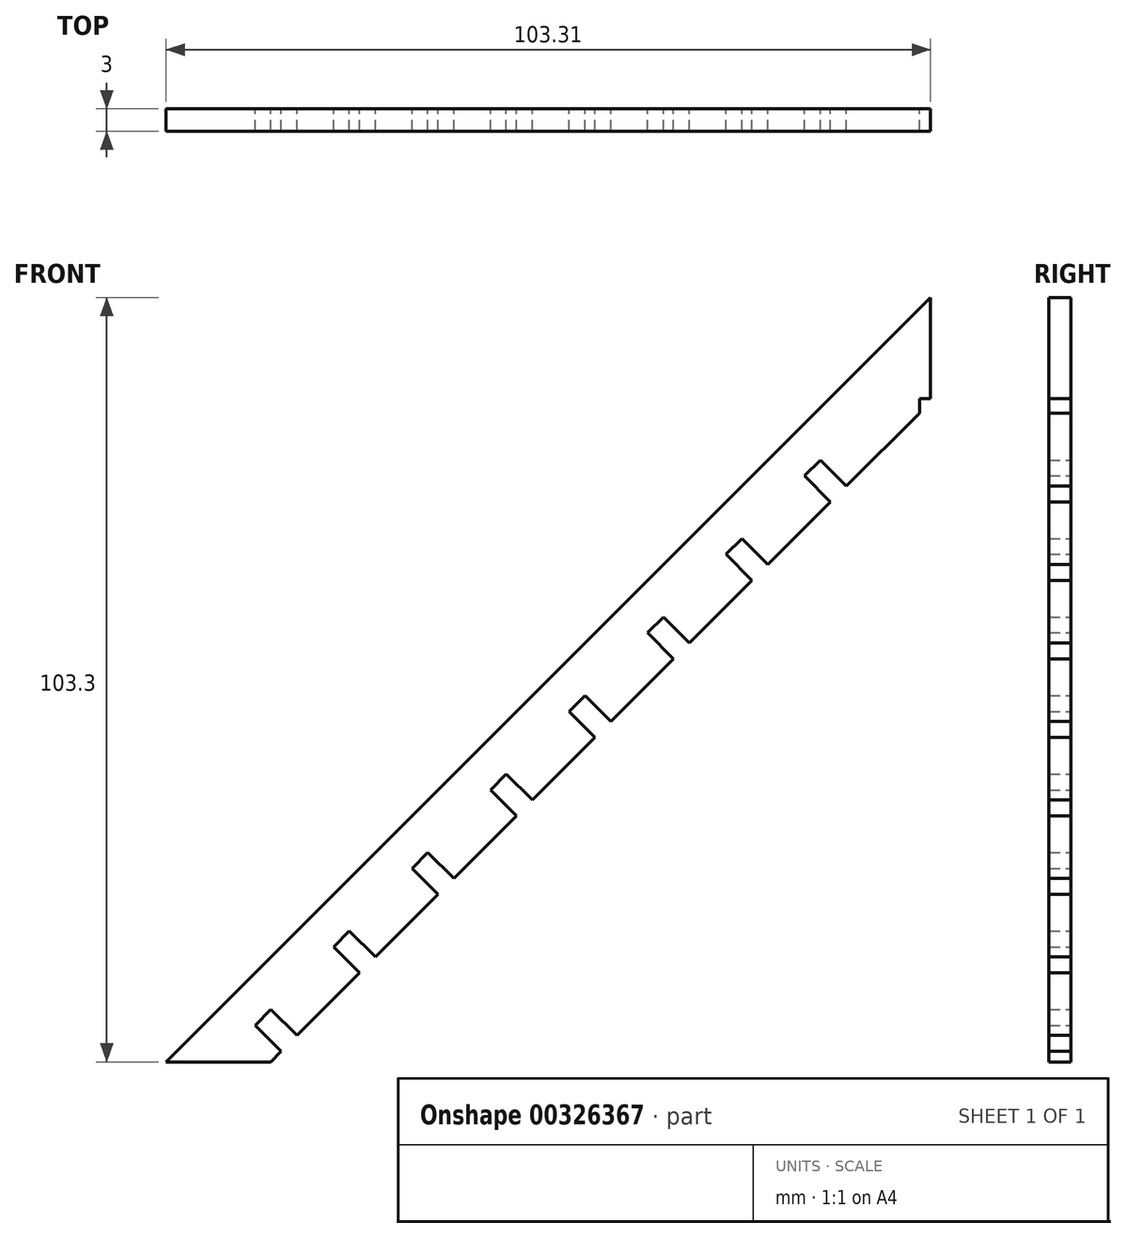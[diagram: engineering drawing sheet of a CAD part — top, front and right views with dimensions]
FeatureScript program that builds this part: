
annotation { "Feature Type Name" : "Feature", "Feature Type Description" : "" }
export const myFeature = defineFeature(function(context is Context, id is Id, definition is map)
    precondition{}
    {
        {
            var Q0;
            Q0=qCreatedBy(makeId("Front.planeOp"),FACE);
            var sketch = newSketch(context, id + "F0", { "sketchPlane" : qUnion([Q0])});
            skLineSegment(sketch, "E0", {"start": v(-78.64, 4.95) * mm, "end": v(-75.1, 1.42) * mm});
            skLineSegment(sketch, "E1", {"start": v(-68.04, 15.56) * mm, "end": v(-64.5, 12.02) * mm});
            skPoint(sketch, "E2", {"position": v(-57.43, 26.16) * mm});
            skPoint(sketch, "E3", {"position": v(-46.82, 36.77) * mm});
            skPoint(sketch, "E4", {"position": v(-36.22, 47.38) * mm});
            skPoint(sketch, "E5", {"position": v(-25.61, 57.98) * mm});
            skPoint(sketch, "E6", {"position": v(-15, 68.59) * mm});
            skPoint(sketch, "E7", {"position": v(-4.4, 79.2) * mm});
            skLineSegment(sketch, "E8", {"start": v(-72.96, 3.56) * mm, "end": v(-76.5, 7.1) * mm});
            skLineSegment(sketch, "E9", {"start": v(-57.43, 26.16) * mm, "end": v(-53.9, 22.63) * mm});
            skLineSegment(sketch, "E10", {"start": v(-46.82, 36.77) * mm, "end": v(-43.29, 33.23) * mm});
            skLineSegment(sketch, "E11", {"start": v(-36.22, 47.38) * mm, "end": v(-32.68, 43.84) * mm});
            skLineSegment(sketch, "E12", {"start": v(-25.61, 57.98) * mm, "end": v(-22.08, 54.45) * mm});
            skLineSegment(sketch, "E13", {"start": v(-15, 68.59) * mm, "end": v(-11.47, 65.05) * mm});
            skLineSegment(sketch, "E14", {"start": v(-4.4, 79.2) * mm, "end": v(-0.86, 75.66) * mm});
            skLineSegment(sketch, "E15", {"start": v(-65.89, 17.7) * mm, "end": v(-62.35, 14.17) * mm});
            skLineSegment(sketch, "E16", {"start": v(-55.28, 28.31) * mm, "end": v(-51.75, 24.78) * mm});
            skLineSegment(sketch, "E17", {"start": v(-44.67, 38.92) * mm, "end": v(-41.14, 35.38) * mm});
            skLineSegment(sketch, "E18", {"start": v(-34.07, 49.53) * mm, "end": v(-30.53, 46) * mm});
            skLineSegment(sketch, "E19", {"start": v(-23.46, 60.13) * mm, "end": v(-19.93, 56.6) * mm});
            skLineSegment(sketch, "E20", {"start": v(-12.85, 70.74) * mm, "end": v(-9.32, 67.2) * mm});
            skLineSegment(sketch, "E21", {"start": v(-2.25, 81.35) * mm, "end": v(1.29, 77.81) * mm});
            skLineSegment(sketch, "E22", {"start": v(-72.96, 3.56) * mm, "end": v(-64.5, 12.02) * mm});
            skLineSegment(sketch, "E23", {"start": v(-62.35, 14.17) * mm, "end": v(-53.9, 22.63) * mm});
            skLineSegment(sketch, "E24", {"start": v(-51.75, 24.78) * mm, "end": v(-43.29, 33.23) * mm});
            skLineSegment(sketch, "E25", {"start": v(-41.14, 35.38) * mm, "end": v(-32.68, 43.84) * mm});
            skLineSegment(sketch, "E26", {"start": v(-30.53, 46) * mm, "end": v(-22.08, 54.45) * mm});
            skLineSegment(sketch, "E27", {"start": v(-19.93, 56.6) * mm, "end": v(-11.47, 65.05) * mm});
            skLineSegment(sketch, "E28", {"start": v(-9.32, 67.2) * mm, "end": v(-0.86, 75.66) * mm});
            skLineSegment(sketch, "E29", {"start": v(-75.1, 1.42) * mm, "end": v(-76.52, 0) * mm});
            skLineSegment(sketch, "E30", {"start": v(-76.52, 0) * mm, "end": v(-90.67, 0) * mm});
            skLineSegment(sketch, "E31", {"start": v(-78.64, 4.95) * mm, "end": v(-76.5, 7.1) * mm});
            skLineSegment(sketch, "E32", {"start": v(-68.04, 15.56) * mm, "end": v(-65.89, 17.7) * mm});
            skLineSegment(sketch, "E33", {"start": v(-55.28, 28.31) * mm, "end": v(-57.43, 26.16) * mm});
            skLineSegment(sketch, "E34", {"start": v(-44.67, 38.92) * mm, "end": v(-46.82, 36.77) * mm});
            skLineSegment(sketch, "E35", {"start": v(-25.61, 57.98) * mm, "end": v(-23.46, 60.13) * mm});
            skLineSegment(sketch, "E36", {"start": v(-36.22, 47.38) * mm, "end": v(-34.07, 49.53) * mm});
            skLineSegment(sketch, "E37", {"start": v(-15, 68.59) * mm, "end": v(-12.85, 70.74) * mm});
            skLineSegment(sketch, "E38", {"start": v(-4.4, 79.2) * mm, "end": v(-2.25, 81.35) * mm});
            skPoint(sketch, "E39", {"position": v(12.16, 90.24) * mm});
            skLineSegment(sketch, "E40", {"start": v(-90.67, 0) * mm, "end": v(12.16, 102.82) * mm});
            skLineSegment(sketch, "E41", {"start": v(267.6, 1.92) * mm, "end": v(276.05, 10.38) * mm});
            skLineSegment(sketch, "E42", {"start": v(265.44, -0.22) * mm, "end": v(256.99, -8.68) * mm});
            skLineSegment(sketch, "E43", {"start": v(259.84, -13.66) * mm, "end": v(254.42, -13.66) * mm});
            skLineSegment(sketch, "E44", {"start": v(254.84, -10.83) * mm, "end": v(256.25, -12.24) * mm});
            skLineSegment(sketch, "E45", {"start": v(256.25, -12.24) * mm, "end": v(258.4, -10.1) * mm});
            skLineSegment(sketch, "E46", {"start": v(266.86, -1.64) * mm, "end": v(269, 0.51) * mm});
            skLineSegment(sketch, "E47", {"start": v(265.44, -0.22) * mm, "end": v(266.86, -1.64) * mm});
            skPoint(sketch, "E48", {"position": v(276.05, 10.38) * mm});
            skPoint(sketch, "E49", {"position": v(286.66, 20.99) * mm});
            skPoint(sketch, "E50", {"position": v(297.26, 31.6) * mm});
            skPoint(sketch, "E51", {"position": v(307.87, 42.2) * mm});
            skPoint(sketch, "E52", {"position": v(318.48, 52.8) * mm});
            skPoint(sketch, "E53", {"position": v(329.08, 63.41) * mm});
            skLineSegment(sketch, "E54", {"start": v(258.4, -10.1) * mm, "end": v(256.99, -8.68) * mm});
            skLineSegment(sketch, "E55", {"start": v(276.05, 10.38) * mm, "end": v(277.46, 8.97) * mm});
            skLineSegment(sketch, "E56", {"start": v(286.66, 20.99) * mm, "end": v(288.07, 19.57) * mm});
            skLineSegment(sketch, "E57", {"start": v(297.26, 31.6) * mm, "end": v(298.68, 30.18) * mm});
            skLineSegment(sketch, "E58", {"start": v(307.87, 42.2) * mm, "end": v(309.28, 40.79) * mm});
            skLineSegment(sketch, "E59", {"start": v(318.48, 52.8) * mm, "end": v(319.89, 51.4) * mm});
            skLineSegment(sketch, "E60", {"start": v(329.08, 63.41) * mm, "end": v(330.5, 62) * mm});
            skLineSegment(sketch, "E61", {"start": v(267.6, 1.92) * mm, "end": v(269, 0.51) * mm});
            skLineSegment(sketch, "E62", {"start": v(278.2, 12.53) * mm, "end": v(279.61, 11.12) * mm});
            skLineSegment(sketch, "E63", {"start": v(288.8, 23.14) * mm, "end": v(290.22, 21.72) * mm});
            skLineSegment(sketch, "E64", {"start": v(299.41, 33.74) * mm, "end": v(300.83, 32.33) * mm});
            skLineSegment(sketch, "E65", {"start": v(310.02, 44.35) * mm, "end": v(311.43, 42.94) * mm});
            skLineSegment(sketch, "E66", {"start": v(320.62, 54.96) * mm, "end": v(322.04, 53.54) * mm});
            skLineSegment(sketch, "E67", {"start": v(331.23, 65.56) * mm, "end": v(332.65, 64.15) * mm});
            skLineSegment(sketch, "E68", {"start": v(342.55, 76.89) * mm, "end": v(344.02, 76.89) * mm});
            skLineSegment(sketch, "E69", {"start": v(344.02, 73.88) * mm, "end": v(344.02, 76.89) * mm});
            skLineSegment(sketch, "E70", {"start": v(345.54, 69.98) * mm, "end": v(345.54, 73.88) * mm});
            skLineSegment(sketch, "E71", {"start": v(344.02, 73.88) * mm, "end": v(345.54, 73.88) * mm});
            skLineSegment(sketch, "E72.trimOffspring", {"start": v(254.84, -10.83) * mm, "end": v(253.71, -11.95) * mm});
            skLineSegment(sketch, "E73.trimOffspring", {"start": v(277.46, 8.97) * mm, "end": v(279.61, 11.12) * mm});
            skLineSegment(sketch, "E74.trimOffspring", {"start": v(278.2, 12.53) * mm, "end": v(286.66, 20.99) * mm});
            skLineSegment(sketch, "E75.trimOffspring", {"start": v(288.07, 19.57) * mm, "end": v(290.22, 21.72) * mm});
            skLineSegment(sketch, "E76.trimOffspring", {"start": v(288.8, 23.14) * mm, "end": v(297.26, 31.6) * mm});
            skLineSegment(sketch, "E77.trimOffspring", {"start": v(298.68, 30.18) * mm, "end": v(300.83, 32.33) * mm});
            skLineSegment(sketch, "E78.trimOffspring", {"start": v(299.41, 33.74) * mm, "end": v(307.87, 42.2) * mm});
            skLineSegment(sketch, "E79.trimOffspring", {"start": v(309.28, 40.79) * mm, "end": v(311.43, 42.94) * mm});
            skLineSegment(sketch, "E80.trimOffspring", {"start": v(310.02, 44.35) * mm, "end": v(318.48, 52.8) * mm});
            skLineSegment(sketch, "E81.trimOffspring", {"start": v(319.89, 51.4) * mm, "end": v(322.04, 53.54) * mm});
            skLineSegment(sketch, "E82.trimOffspring", {"start": v(320.62, 54.96) * mm, "end": v(329.08, 63.41) * mm});
            skLineSegment(sketch, "E83.trimOffspring", {"start": v(330.5, 62) * mm, "end": v(332.65, 64.15) * mm});
            skLineSegment(sketch, "E84.trimOffspring", {"start": v(331.23, 65.56) * mm, "end": v(342.55, 76.89) * mm});
            skLineSegment(sketch, "E85", {"start": v(275, -0.57) * mm, "end": v(331.6, 56.03) * mm});
            skPoint(sketch, "E86.visualSharp", {"position": v(252, -13.66) * mm});
            skArc(sketch, "E86.filletArc", {"start": v(253.71, -11.95) * mm, "mid": v(253.5, -13.04) * mm, "end": v(254.42, -13.66) * mm});
            skPoint(sketch, "E87.visualSharp", {"position": v(262.1, -13.66) * mm});
            skArc(sketch, "E87.filletArc", {"start": v(259.84, -13.66) * mm, "mid": v(261.82, -13.25) * mm, "end": v(263.48, -12.1) * mm});
            skPoint(sketch, "E88", {"position": v(267.53, -3.28) * mm});
            skLineSegment(sketch, "E89", {"start": v(263.48, -12.1) * mm, "end": v(266.65, -8.91) * mm});
            skLineSegment(sketch, "E90", {"start": v(267.53, -3.28) * mm, "end": v(267.53, -6.8) * mm});
            skLineSegment(sketch, "E91", {"start": v(275, -0.57) * mm, "end": v(270.91, -4.65) * mm});
            skLineSegment(sketch, "E92", {"start": v(267.53, -3.28) * mm, "end": v(270.57, -3.28) * mm});
            skLineSegment(sketch, "E93", {"start": v(270.57, -3.28) * mm, "end": v(270.57, -4.51) * mm});
            skPoint(sketch, "E94.endSnap0", {"position": v(269.05, -3.28) * mm});
            skPoint(sketch, "E95", {"position": v(272.28, -3.28) * mm});
            skPoint(sketch, "E96.visualSharp", {"position": v(267.53, -8.03) * mm});
            skArc(sketch, "E96.filletArc", {"start": v(266.65, -8.91) * mm, "mid": v(267.3, -7.94) * mm, "end": v(267.53, -6.8) * mm});
            skPoint(sketch, "E97.visualSharp", {"position": v(270.57, -5) * mm});
            skArc(sketch, "E97.filletArc", {"start": v(270.57, -4.51) * mm, "mid": v(270.7, -4.7) * mm, "end": v(270.91, -4.65) * mm});
            skPoint(sketch, "E98", {"position": v(340.52, 64.96) * mm});
            skLineSegment(sketch, "E99.trimOffspring", {"start": v(343.56, 68) * mm, "end": v(345.54, 69.98) * mm});
            skLineSegment(sketch, "E100", {"start": v(340.18, 64.62) * mm, "end": v(343.56, 68) * mm});
            skPoint(sketch, "E101", {"position": v(330.93, 56.37) * mm});
            skPoint(sketch, "E102", {"position": v(330.93, 59.4) * mm});
            skLineSegment(sketch, "E103", {"start": v(330.93, 59.4) * mm, "end": v(334.56, 59.4) * mm});
            skLineSegment(sketch, "E104", {"start": v(330.93, 59.4) * mm, "end": v(330.93, 56.37) * mm});
            skLineSegment(sketch, "E105", {"start": v(330.93, 56.37) * mm, "end": v(331.45, 56.37) * mm});
            skLineSegment(sketch, "E106.trimOffspring", {"start": v(335.27, 59.7) * mm, "end": v(340.18, 64.62) * mm});
            skPoint(sketch, "E107.visualSharp", {"position": v(331.93, 56.37) * mm});
            skArc(sketch, "E107.filletArc", {"start": v(331.6, 56.03) * mm, "mid": v(331.64, 56.24) * mm, "end": v(331.45, 56.37) * mm});
            skPoint(sketch, "E108.visualSharp", {"position": v(334.97, 59.4) * mm});
            skArc(sketch, "E108.filletArc", {"start": v(334.56, 59.4) * mm, "mid": v(334.94, 59.48) * mm, "end": v(335.27, 59.7) * mm});
            skLineSegment(sketch, "E109", {"start": v(344.02, 74.46) * mm, "end": v(345.54, 74.46) * mm});
            skPoint(sketch, "E110", {"position": v(-0.83, 79.93) * mm});
            skLineSegment(sketch, "E111", {"start": v(1.29, 77.81) * mm, "end": v(10.64, 87.16) * mm});
            skPoint(sketch, "E112.orphan", {"position": v(12.16, 88.68) * mm});
            skLineSegment(sketch, "E113", {"start": v(12.64, 89.63) * mm, "end": v(12.64, 109.16) * mm});
            skLineSegment(sketch, "E114", {"start": v(10.64, 87.16) * mm, "end": v(11.16, 87.68) * mm});
            skLineSegment(sketch, "E115", {"start": v(12.16, 102.82) * mm, "end": v(12.64, 103.3) * mm});
            skLineSegment(sketch, "E116", {"start": v(11.16, 88.68) * mm, "end": v(11.16, 87.68) * mm});
            skLineSegment(sketch, "E117", {"start": v(11.16, 88.68) * mm, "end": v(11.16, 89.63) * mm});
            skLineSegment(sketch, "E118", {"start": v(11.16, 89.63) * mm, "end": v(12.64, 89.63) * mm});
            skSolve(sketch);
        }
        {
            var Q0;
            Q0=makeQuery(id+"F0.imprint","IMPRINT",FACE,{"disambiguationData":[TD([[makeQuery(id+"F0.imprint","IMPRINT",EDGE,{"derivedFrom":sQuery(id+"F0.wireOp",EDGE,"E0")}),-1.0]])]});
            extrude(context, id + "F1", {"entities" : qUnion([Q0]), "depth" : 3 * mm});
        }
    });
